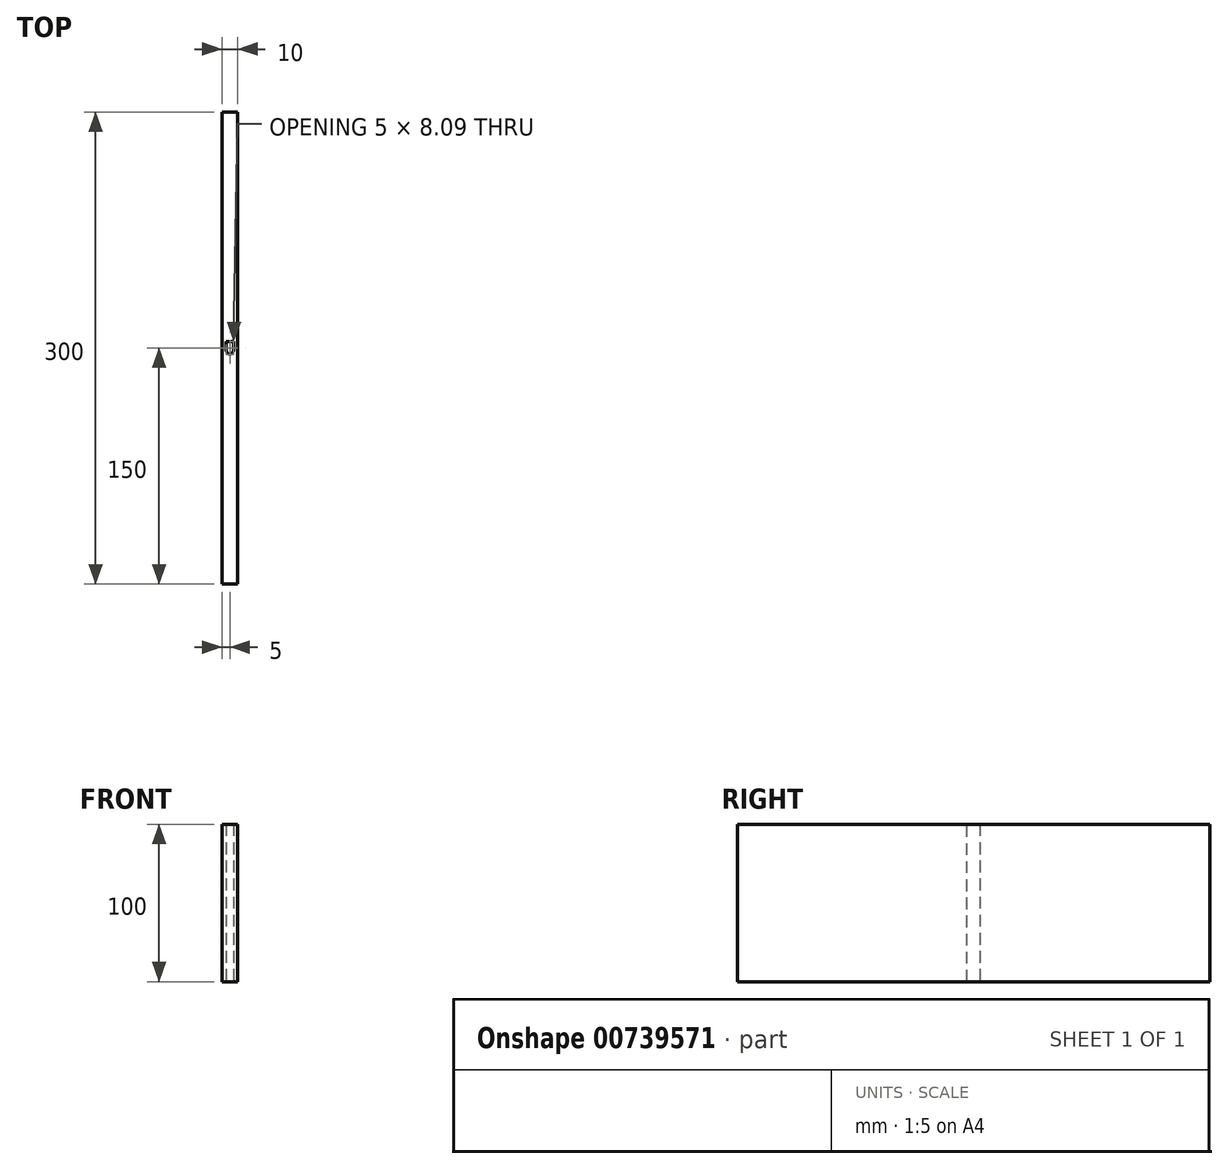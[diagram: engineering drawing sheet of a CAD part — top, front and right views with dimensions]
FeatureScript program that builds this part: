
annotation { "Feature Type Name" : "Feature", "Feature Type Description" : "" }
export const myFeature = defineFeature(function(context is Context, id is Id, definition is map)
    precondition{}
    {
        {
            assignVariable(context, id + "F0", {"name" : "h", "anyValue" : 100 * mm});
        }
        {
            var Q0;
            Q0=qCreatedBy(makeId("Top.planeOp"),FACE);
            var sketch = newSketch(context, id + "F1", { "sketchPlane" : qUnion([Q0])});
            skLineSegment(sketch, "E0.bottom", {"start": v(5, 150) * mm, "end": v(-5, 150) * mm});
            skLineSegment(sketch, "E0.top", {"start": v(5, -150) * mm, "end": v(-5, -150) * mm});
            skLineSegment(sketch, "E0.left", {"start": v(5, 150) * mm, "end": v(5, -150) * mm});
            skLineSegment(sketch, "E0.right", {"start": v(-5, 150) * mm, "end": v(-5, -150) * mm});
            skPoint(sketch, "E0.middle", {"position": v(0, 0) * mm});
            skLineSegment(sketch, "E1", {"start": v(0, 150) * mm, "end": v(0, -150) * mm});
            skEllipse(sketch, "E2", {"center": v(5, 0) * mm, "majorRadius": 4.04 * mm, "minorRadius": 2.5 * mm, "majorAxis": v(0, 1)});
            skLineSegment(sketch, "E3", {"start": v(2.5, 0) * mm, "end": v(2.5, -4.04) * mm});
            skLineSegment(sketch, "E4", {"start": v(5, -4.04) * mm, "end": v(2.5, -4.04) * mm});
            skPoint(sketch, "E5", {"position": v(7.5, 0) * mm});
            skPoint(sketch, "E6", {"position": v(5, 4.05) * mm});
            skSolve(sketch);
        }
        {
            var Q0;
            {var subQ8=sQuery(id+"F1.wireOp",EDGE,"E1");Q0=makeQuery(id+"F1.imprint","IMPRINT",FACE,{"disambiguationData":[TD([[makeQuery(id+"F1.imprint","IMPRINT",EDGE,{"derivedFrom":subQ8}),1.0]])]});}
            extrude(context, id + "F2", {"entities" : qUnion([Q0]), "depth" : getVariable(context, 'h'), "offsetDistance" : 25 * mm});
        }
        {
            var Q0;
            Q0=sQuery(id+"F1.wireOp",EDGE,"E0.left");
            cPoint(context, id + "F3", {"entities" : qUnion([Q0]), "parameter" : 0.5});
        }
        {
            var Q0;
            Q0=makeQuery(id+"F2.opExtrude","SWEPT_BODY",BODY,{"disambiguationData":[OSD([sQuery(id+"F1.wireOp",EDGE,"E0.bottom"),sQuery(id+"F1.wireOp",EDGE,"E0.top"),sQuery(id+"F1.wireOp",EDGE,"E0.left"),sQuery(id+"F1.wireOp",EDGE,"E1"),sQuery(id+"F1.wireOp",EDGE,"E2"),sQuery(id+"F1.wireOp",EDGE,"E3"),sQuery(id+"F1.wireOp",EDGE,"E4")])]});
            var Q1;
            Q1=qCreatedBy(id+"F3",VERTEX);
            var Q2;
            Q2=sQuery(id+"F1.wireOp",VERTEX,"E0.middle");
            transform(context, id + "F4", {"entities" : qUnion([Q0]), "transformType" : TransformType.TRANSLATION_ENTITY, "oppositeDirectionEntity" : false, "transformLine" : qUnion([Q1, Q2]), "makeCopy" : false});
        }
        {
            var Q0;
            Q0=makeQuery(id+"F2.opExtrude","SWEPT_BODY",BODY,{"disambiguationData":[OSD([sQuery(id+"F1.wireOp",EDGE,"E0.bottom"),sQuery(id+"F1.wireOp",EDGE,"E0.top"),sQuery(id+"F1.wireOp",EDGE,"E0.left"),sQuery(id+"F1.wireOp",EDGE,"E1"),sQuery(id+"F1.wireOp",EDGE,"E2"),sQuery(id+"F1.wireOp",EDGE,"E3"),sQuery(id+"F1.wireOp",EDGE,"E4")])]});
            var Q1;
            Q1=qCreatedBy(makeId("Right.planeOp"),FACE);
            mirror(context, id + "F5", {"operationType" : NewBodyOperationType.ADD, "entities" : qUnion([Q0]), "mirrorPlane" : qUnion([Q1])});
        }
        {
            var Q0;
            Q0=makeQuery(id+"F2.opExtrude","SWEPT_BODY",BODY,{"disambiguationData":[OSD([sQuery(id+"F1.wireOp",EDGE,"E0.bottom"),sQuery(id+"F1.wireOp",EDGE,"E0.top"),sQuery(id+"F1.wireOp",EDGE,"E0.left"),sQuery(id+"F1.wireOp",EDGE,"E1"),sQuery(id+"F1.wireOp",EDGE,"E2"),sQuery(id+"F1.wireOp",EDGE,"E3"),sQuery(id+"F1.wireOp",EDGE,"E4")])]});
            var Q1;
            Q1=makeQuery(id+"F5.opPattern","COPY",EDGE,{"derivedFrom":makeQuery(id+"F2.opExtrude","SWEPT_EDGE",EDGE,{"disambiguationData":[OSD([sQuery(id+"F1.wireOp",EDGE,"E0.top"),sQuery(id+"F1.wireOp",EDGE,"E1")])]}),"instanceName":"1"});
            transform(context, id + "F6", {"entities" : qUnion([Q0]), "transformType" : TransformType.ROTATION, "transformAxis" : qUnion([Q1]), "angle" : 180 * degree, "makeCopy" : false});
        }
        {
            var Q0;
            {var subQ0=makeQuery(id+"F2.opExtrude","CAP_FACE",FACE,{"disambiguationData":[OSD([sQuery(id+"F1.wireOp",EDGE,"E0.bottom"),sQuery(id+"F1.wireOp",EDGE,"E0.top"),sQuery(id+"F1.wireOp",EDGE,"E0.left"),sQuery(id+"F1.wireOp",EDGE,"E1"),sQuery(id+"F1.wireOp",EDGE,"E2"),sQuery(id+"F1.wireOp",EDGE,"E3"),sQuery(id+"F1.wireOp",EDGE,"E4")])],"isStart":true});Q0=makeQuery(id+"F5.boolean.opBoolean","MERGE",FACE,{"derivedFrom":[subQ0,makeQuery(id+"F5.opPattern","COPY",FACE,{"derivedFrom":subQ0,"instanceName":"1"})]});}
            var sketch = newSketch(context, id + "F7", { "sketchPlane" : qUnion([Q0])});
            skLineSegment(sketch, "E7", {"start": v(12.5, 300) * mm, "end": v(7.5, 300) * mm});
            skLineSegment(sketch, "E8", {"start": v(10, 295.95) * mm, "end": v(10, 304.04) * mm});
            skPoint(sketch, "E9", {"position": v(10, 300) * mm});
            skSolve(sketch);
        }
        {
            var Q0;
            Q0=sQuery(id+"F7.wireOp",EDGE,"E8");
            cPoint(context, id + "F8", {"entities" : qUnion([Q0]), "parameter" : 0.5});
        }
        {
            var Q0;
            Q0=makeQuery(id+"F2.opExtrude","SWEPT_BODY",BODY,{"disambiguationData":[OSD([sQuery(id+"F1.wireOp",EDGE,"E0.bottom"),sQuery(id+"F1.wireOp",EDGE,"E0.top"),sQuery(id+"F1.wireOp",EDGE,"E0.left"),sQuery(id+"F1.wireOp",EDGE,"E1"),sQuery(id+"F1.wireOp",EDGE,"E2"),sQuery(id+"F1.wireOp",EDGE,"E3"),sQuery(id+"F1.wireOp",EDGE,"E4")])]});
            var Q1;
            Q1=qCreatedBy(id+"F8",VERTEX);
            var Q2;
            Q2=qCreatedBy(makeId("Origin.pointOp"),VERTEX);
            transform(context, id + "F9", {"entities" : qUnion([Q0]), "transformType" : TransformType.TRANSLATION_ENTITY, "oppositeDirectionEntity" : false, "transformLine" : qUnion([Q1, Q2]), "makeCopy" : false});
        }
    });
